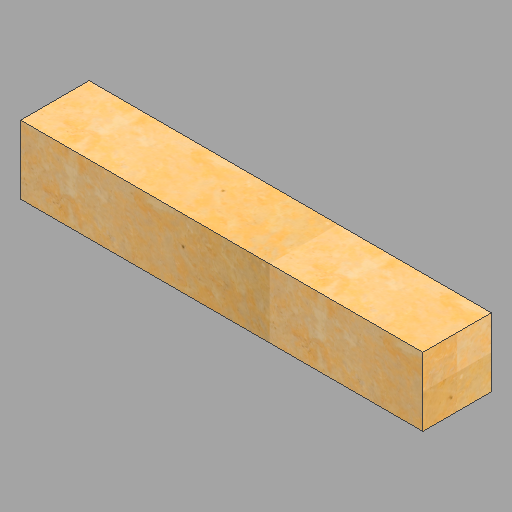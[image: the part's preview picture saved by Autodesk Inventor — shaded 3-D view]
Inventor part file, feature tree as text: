
AUTODESK INVENTOR PART (.ipt)
format: ipt  version: 2023 (Build 270158030, 158C)  size: 243,200 bytes
history: native  units: in
note: dims shown in document units (in); Inventor stores cm internally (conversion verified against a paired STEP export)
features: extrude x1, sketch x1
ambient origin geometry x8: Origin, YZ Plane, XZ Plane, XY Plane, X Axis, Y Axis, Z Axis, Center Point
bodies: Solid1 (feature_tree)
feature tree (2):
  extrude  "Extrusion1"  Depth=8.0in
  sketch  "Sketch1"  dims[d0=8.0in d1=8.0in d2=47.0in d3=0.0in]
